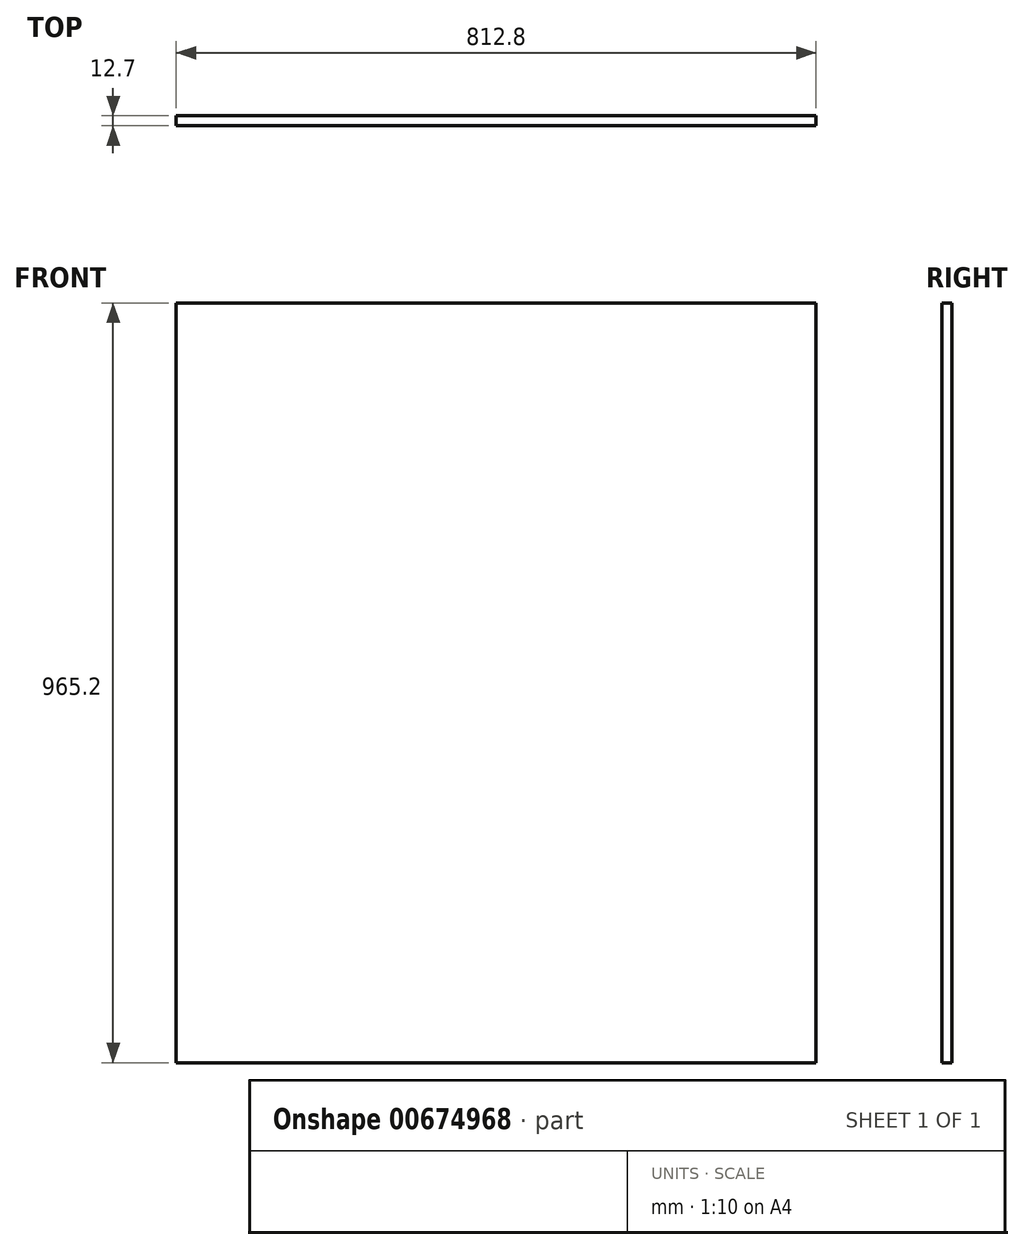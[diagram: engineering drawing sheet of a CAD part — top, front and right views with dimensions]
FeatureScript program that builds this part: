
annotation { "Feature Type Name" : "Feature", "Feature Type Description" : "" }
export const myFeature = defineFeature(function(context is Context, id is Id, definition is map)
    precondition{}
    {
        {
            var Q0;
            Q0=qCreatedBy(makeId("Front.planeOp"),FACE);
            var sketch = newSketch(context, id + "F0", { "sketchPlane" : qUnion([Q0])});
            skLineSegment(sketch, "E0.bottom", {"start": v(0, 0) * mm, "end": v(812.8, 0) * mm});
            skLineSegment(sketch, "E0.top", {"start": v(0, 965.2) * mm, "end": v(812.8, 965.2) * mm});
            skLineSegment(sketch, "E0.left", {"start": v(0, 0) * mm, "end": v(0, 965.2) * mm});
            skLineSegment(sketch, "E0.right", {"start": v(812.8, 0) * mm, "end": v(812.8, 965.2) * mm});
            skSolve(sketch);
        }
        {
            var Q0;
            Q0 = qSketchRegion(id + "F0", true);
            extrude(context, id + "F1", {"entities" : qUnion([Q0]), "depth" : 12.7 * mm, "offsetDistance" : 25.4 * mm});
        }
    });
